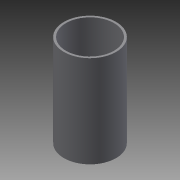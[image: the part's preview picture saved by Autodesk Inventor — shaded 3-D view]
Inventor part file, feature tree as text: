
AUTODESK INVENTOR PART (.ipt)
format: ipt  version: 2014 SP2 (Build 180246200, 246)  size: 119,296 bytes
history: native  units: in
note: dims shown in document units (in); Inventor stores cm internally (conversion verified against a paired STEP export)
features: other x84, revolve x1, sketch x1
ambient origin geometry x8: Origin, YZ Plane, XZ Plane, XY Plane, X Axis, Y Axis, Z Axis, Center Point
bodies: Solid1 (feature_tree)
feature tree (86):
  revolve  "Revolution1"  [1 undecoded]
  other  "rod_to_part_XY"
  other  "rod_to_part_YZ"
  other  "rod_to_part_ZX"
  other  "rod_to_part_X"
  other  "rod_to_part_Y"
  other  "rod_to_part_Z"
  other  "rod_to_part_Center"
  other  "to_road_XY"
  other  "to_road_YZ"
  other  "to_road_ZX"
  other  "to_road_X"
  other  "to_road_Y"
  other  "to_road_Z"
  other  "to_road_Center"
  other  "track1_XY"
  other  "track1_YZ"
  other  "track1_ZX"
  other  "track1_X"
  other  "track1_Y"
  other  "track1_Z"
  other  "track1_Center"
  other  "track1_u_XY"
  other  "track1_u_YZ"
  other  "track1_u_ZX"
  other  "track1_u_X"
  other  "track1_u_Y"
  other  "track1_u_Z"
  other  "track1_u_Center"
  other  "track2_XY"
  other  "track2_YZ"
  other  "track2_ZX"
  other  "track2_X"
  other  "track2_Y"
  other  "track2_Z"
  other  "track2_Center"
  other  "track2_u_XY"
  other  "track2_u_YZ"
  other  "track2_u_ZX"
  other  "track2_u_X"
  other  "track2_u_Y"
  other  "track2_u_Z"
  other  "track2_u_Center"
  other  "track3_XY"
  other  "track3_YZ"
  other  "track3_ZX"
  other  "track3_X"
  other  "track3_Y"
  other  "track3_Z"
  other  "track3_Center"
  other  "track3_u_XY"
  other  "track3_u_YZ"
  other  "track3_u_ZX"
  other  "track3_u_X"
  other  "track3_u_Y"
  other  "track3_u_Z"
  other  "track3_u_Center"
  other  "track4_XY"
  other  "track4_YZ"
  other  "track4_ZX"
  other  "track4_X"
  other  "track4_Y"
  other  "track4_Z"
  other  "track4_Center"
  other  "track4_u_XY"
  other  "track4_u_YZ"
  other  "track4_u_ZX"
  other  "track4_u_X"
  other  "track4_u_Y"
  other  "track4_u_Z"
  other  "track4_u_Center"
  other  "tube_rear_XY"
  other  "tube_rear_YZ"
  other  "tube_rear_ZX"
  other  "tube_rear_X"
  other  "tube_rear_Y"
  other  "tube_rear_Z"
  other  "tube_rear_Center"
  other  "tube_rod_guide_XY"
  other  "tube_rod_guide_YZ"
  other  "tube_rod_guide_ZX"
  other  "tube_rod_guide_X"
  other  "tube_rod_guide_Y"
  other  "tube_rod_guide_Z"
  other  "tube_rod_guide_Center"
  sketch  "Sketch_4"  dims[d0=360.0deg d1=0.0in d2=0.0in]
note: 1 required parameter value undecoded (feature->parameter linkage not recoverable at this tier; creation-order binding heuristic only, values carry confidence <= 0.55)
